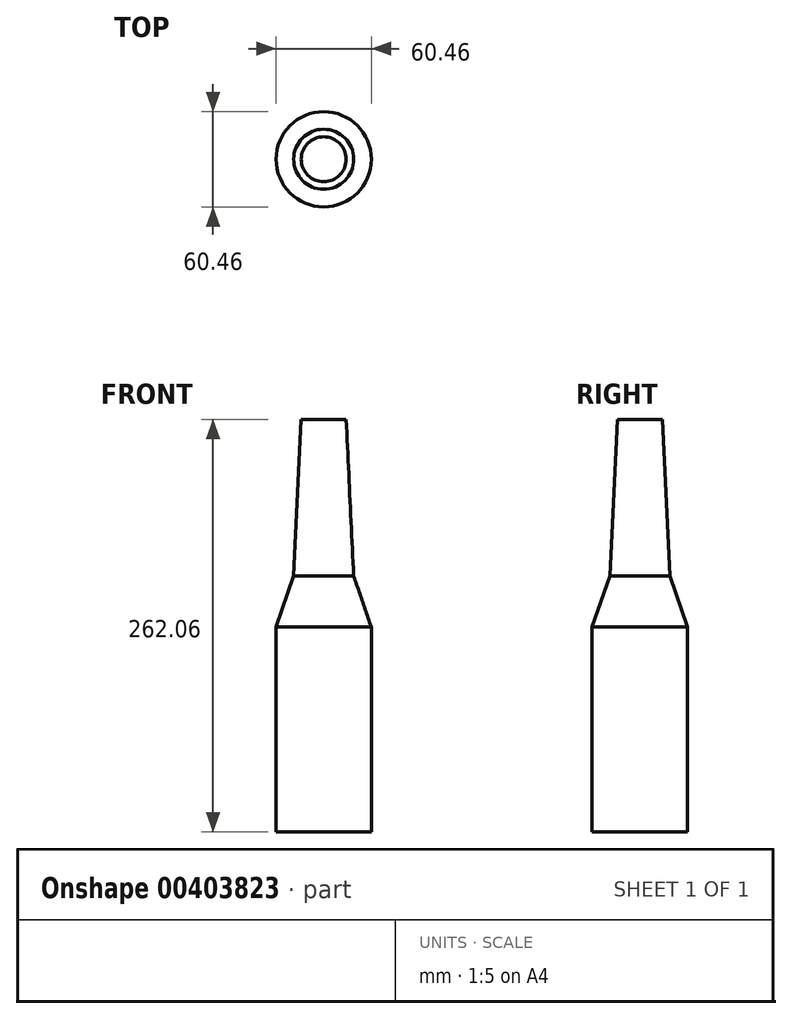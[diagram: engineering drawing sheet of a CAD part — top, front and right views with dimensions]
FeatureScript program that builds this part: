
annotation { "Feature Type Name" : "Feature", "Feature Type Description" : "" }
export const myFeature = defineFeature(function(context is Context, id is Id, definition is map)
    precondition{}
    {
        {
            var Q0;
            Q0=qCreatedBy(makeId("Front.planeOp"),FACE);
            var sketch = newSketch(context, id + "F0", { "sketchPlane" : qUnion([Q0])});
            skLineSegment(sketch, "E0", {"start": v(0, 159.1) * mm, "end": v(0, -164.3) * mm, "construction": true});
            skLineSegment(sketch, "E1", {"start": v(0, 118.58) * mm, "end": v(-14.29, 118.58) * mm});
            skLineSegment(sketch, "E2", {"start": v(-14.29, 118.58) * mm, "end": v(-19.05, 19.1) * mm});
            skLineSegment(sketch, "E3", {"start": v(-19.05, 19.1) * mm, "end": v(-30.23, -13.3) * mm});
            skLineSegment(sketch, "E4", {"start": v(-30.23, -13.3) * mm, "end": v(-30.23, -143.48) * mm});
            skLineSegment(sketch, "E5", {"start": v(-30.23, -143.48) * mm, "end": v(0, -143.48) * mm});
            skLineSegment(sketch, "E6", {"start": v(0, 118.58) * mm, "end": v(0, -143.48) * mm});
            skSolve(sketch);
        }
        {
            var Q0;
            Q0=makeQuery(id+"F0.imprint","IMPRINT",FACE,{"disambiguationData":[TD([[makeQuery(id+"F0.imprint","IMPRINT",EDGE,{"derivedFrom":sQuery(id+"F0.wireOp",EDGE,"E1")}),1.0]])]});
            var Q1;
            Q1=sQuery(id+"F0.wireOp",EDGE,"E0");
            revolve(context, id + "F1", {"entities" : qUnion([Q0]), "axis" : qUnion([Q1]), "revolveType" : RevolveType.FULL});
        }
    });
